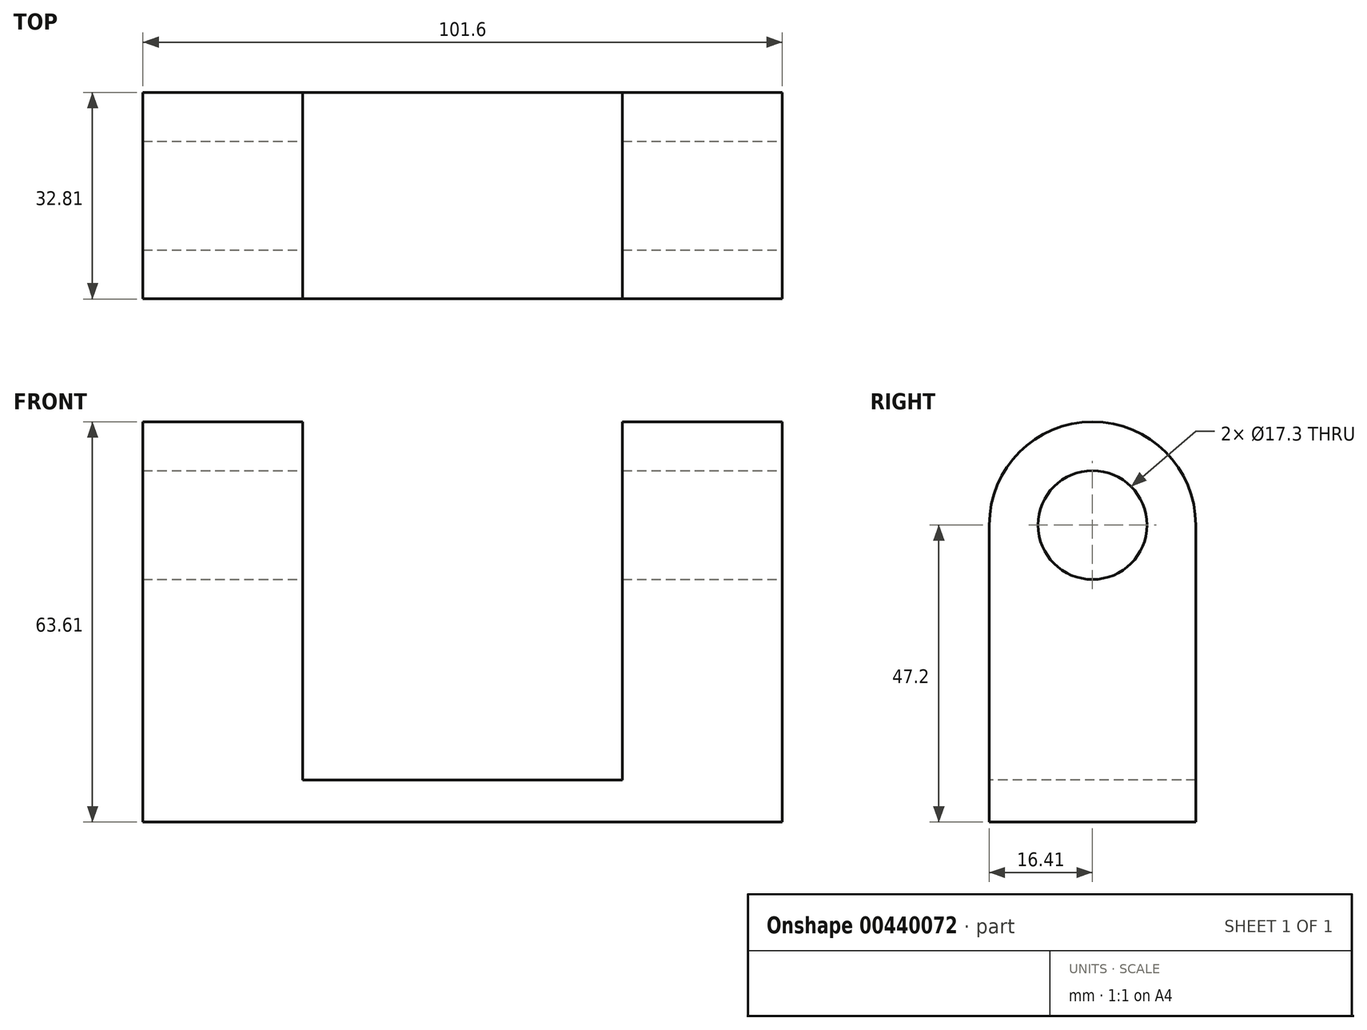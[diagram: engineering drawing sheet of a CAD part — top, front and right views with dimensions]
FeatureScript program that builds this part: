
annotation { "Feature Type Name" : "Feature", "Feature Type Description" : "" }
export const myFeature = defineFeature(function(context is Context, id is Id, definition is map)
    precondition{}
    {
        {
            var Q0;
            Q0=qCreatedBy(makeId("Right.planeOp"),FACE);
            var sketch = newSketch(context, id + "F0", { "sketchPlane" : qUnion([Q0])});
            skLineSegment(sketch, "E0.bottom", {"start": v(-15.69, -9.2) * mm, "end": v(17.12, -9.2) * mm});
            skLineSegment(sketch, "E0.top", {"start": v(-15.69, 38) * mm, "end": v(17.12, 38) * mm});
            skLineSegment(sketch, "E0.left", {"start": v(-15.69, -9.2) * mm, "end": v(-15.69, 38) * mm});
            skLineSegment(sketch, "E0.right", {"start": v(17.12, -9.2) * mm, "end": v(17.12, 38) * mm});
            skCircle(sketch, "E1", {"center": v(0.72, 38) * mm, "radius": 16.4 * mm});
            skCircle(sketch, "E2", {"center": v(0.72, 38) * mm, "radius": 8.65 * mm});
            skSolve(sketch);
        }
        {
            var Q0;
            Q0 = qSketchRegion(id + "F0", true);
            extrude(context, id + "F1", {"entities" : qUnion([Q0]), "oppositeDirection" : true, "depth" : 101.6 * mm});
        }
        {
            var Q0;
            Q0=makeQuery(id+"F1.opExtrude","SWEPT_FACE",FACE,{"disambiguationData":[OSD([sQuery(id+"F0.wireOp",EDGE,"E0.left")])]});
            var sketch = newSketch(context, id + "F2", { "sketchPlane" : qUnion([Q0])});
            skLineSegment(sketch, "E3.top", {"start": v(-76.2, -2.53) * mm, "end": v(-25.4, -2.53) * mm});
            skLineSegment(sketch, "E3.left", {"start": v(-76.2, 38) * mm, "end": v(-76.2, -2.53) * mm});
            skLineSegment(sketch, "E3.right", {"start": v(-25.4, 38) * mm, "end": v(-25.4, -2.53) * mm});
            skLineSegment(sketch, "E4", {"start": v(-76.2, 38) * mm, "end": v(-76.2, 66.88) * mm});
            skLineSegment(sketch, "E5", {"start": v(-76.2, 66.88) * mm, "end": v(-25.4, 66.88) * mm});
            skLineSegment(sketch, "E6", {"start": v(-25.4, 66.88) * mm, "end": v(-25.4, 38) * mm});
            skSolve(sketch);
        }
        {
            var Q0;
            Q0 = qSketchRegion(id + "F2", true);
            extrude(context, id + "F3", {"entities" : qUnion([Q0]), "operationType" : NewBodyOperationType.REMOVE, "endBound" : BoundingType.THROUGH_ALL, "oppositeDirection" : true, "depth" : 25.4 * mm});
        }
    });
